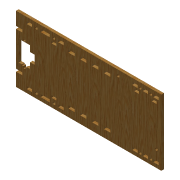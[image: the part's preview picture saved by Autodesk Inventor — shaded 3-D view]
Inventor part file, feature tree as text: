
AUTODESK INVENTOR PART (.ipt)
format: ipt  version: 2016 (Build 200138000, 138)  size: 423,936 bytes
history: native  units: mm
features: extrude x12, sketch x9, mirror x6, plane x5, imported_body x1
ambient origin geometry x8: Origin, YZ Plane, XZ Plane, XY Plane, X Axis, Y Axis, Z Axis, Center Point
bodies: Solid1 (feature_tree)
feature tree (33):
  extrude  "Extrusion1"  Depth=75.0mm
  extrude  "Extrusion2"  Depth=6.0mm
  plane  "Work Plane1"
  plane  "Work Plane2"
  mirror  "Mirror3"
  extrude  "Extrusion4"  Depth=4.0mm
  extrude  "Extrusion5"  Depth=4.0mm TaperAngle=0.0deg
  extrude  "Extrusion6"  [1 undecoded]
  mirror  "Mirror7"
  extrude  "Extrusion7"  Depth=65.0mm
  mirror  "Mirror8"
  extrude  "Extrusion8"  Depth=38.0mm
  extrude  "Extrusion9"  Depth=2.0mm
  extrude  "Extrusion10"  Depth=3.0mm
  mirror  "Mirror9"
  extrude  "Extrusion11"  Depth=3.0mm
  extrude  "Extrusion12"  Depth=3.0mm
  mirror  "Mirror10"
  extrude  "Extrusion13"  Depth=3.0mm
  mirror  "Mirror11"
  imported_body  "Base"
  sketch  "Sketch5"  dims[d0=150.0mm d1=75.0mm]
  sketch  "Sketch6"  dims[d2=3.0mm d3=0.0mm d4=6.0mm]
  sketch  "Sketch7"  dims[d5=3.0mm d6=4.0mm]
  plane  "Work Plane3"
  sketch  "Sketch8"  dims[d7=3.0mm d8=4.0mm d9=0.0mm]
  plane  "Work Plane4"
  plane  "Work Plane5"
  sketch  "Sketch9"  dims[d10=-75.0mm d11=-37.5mm]
  sketch  "Sketch11"  dims[d29=53.0mm d30=65.0mm]
  sketch  "Sketch12"  dims[d31=3.5mm d32=38.0mm]
  sketch  "Sketch13"  dims[d33=3.0mm d34=2.0mm]
  sketch  "Sketch14"  dims[d35=13.0mm d36=3.0mm d37=3.0mm d38=3.0mm d39=3.0mm d40=3.2mm d41=15.0mm d42=50.5mm d43=3.2mm d44=65.5mm d45=7.0mm d46=3.2mm d47=4.0mm d48=0.0mm d49=5.5mm d50=2.5mm d51=2.5mm d52=2.25mm d53=5.5mm d54=2.5mm d57=4.0mm d58=0.0mm d59=7.0mm d60=3.0mm d61=58.0mm d62=8.500035mm d63=4.0mm d64=0.0mm d65=7.0mm d66=3.0mm d67=6.5mm d68=4.0mm d69=0.0mm d70=15.0mm d71=0.0mm d74=3.0mm d75=75.0mm d76=26.0mm d77=4.0mm d78=0.0mm d83=13.0mm d84=13.0mm d85=5.0mm d86=10.0mm d89=6.75mm d91=6.0mm d92=3.0mm d93=6.0mm d94=4.0mm d95=0.0mm d96=12.061494mm d97=4.0mm d99=4.0mm d100=6.0mm d101=6.0mm d102=6.0mm d103=6.0mm d104=3.0mm d105=2.5mm d106=1.75mm d107=3.0mm d108=3.0mm d109=3.0mm d110=3.0mm d111=3.0mm d112=3.0mm d117=2.5mm d118=6.5mm d119=1.8mm d122=0.0mm d124=3.0mm d125=0.0mm d126=4.0mm d129=3.0mm d130=7.0mm d131=2.9mm d132=15.0mm d133=7.0mm d134=2.9mm d135=15.0mm d136=10.0mm d137=0.0mm d138=5.5mm d139=2.5mm d140=2.5mm d141=2.75mm d142=10.0mm d143=0.0mm d144=7.0mm d145=7.0mm d146=6.5mm d147=6.5mm d148=10.0mm d149=0.0mm]
note: 1 required parameter value undecoded (feature->parameter linkage not recoverable at this tier; creation-order binding heuristic only, values carry confidence <= 0.55)
